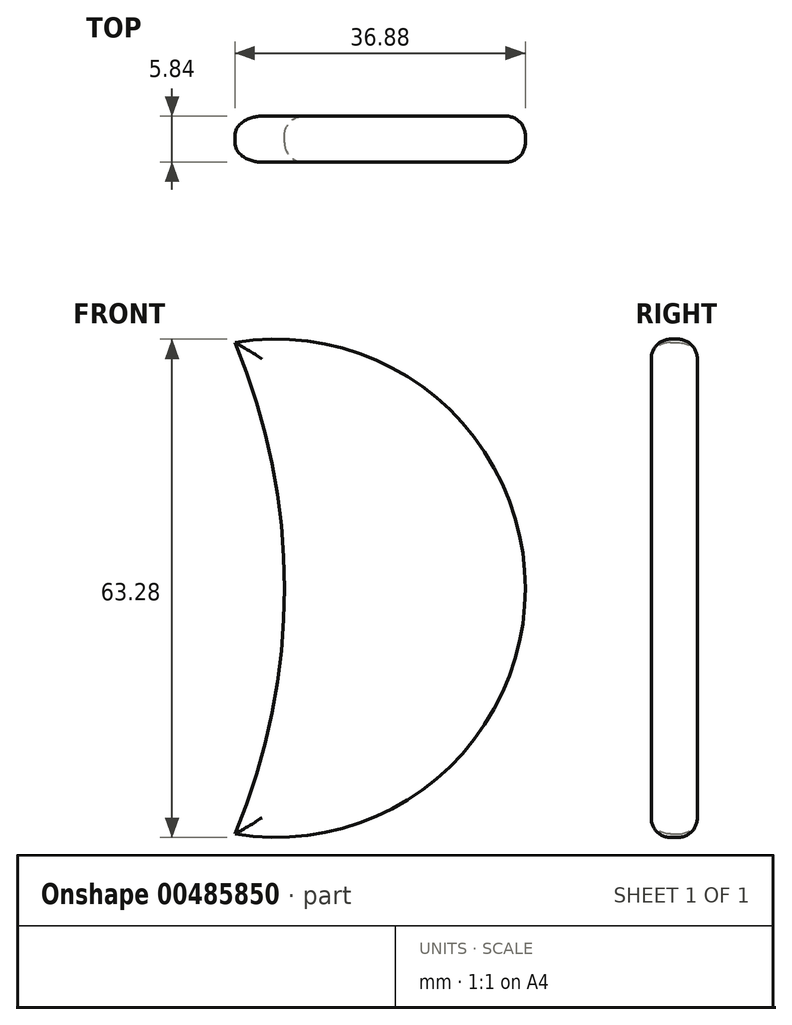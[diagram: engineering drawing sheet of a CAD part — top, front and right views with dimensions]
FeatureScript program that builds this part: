
annotation { "Feature Type Name" : "Feature", "Feature Type Description" : "" }
export const myFeature = defineFeature(function(context is Context, id is Id, definition is map)
    precondition{}
    {
        {
            var Q0;
            Q0=qCreatedBy(makeId("Front.planeOp"),FACE);
            var sketch = newSketch(context, id + "F0", { "sketchPlane" : qUnion([Q0])});
            skArc(sketch, "E0", {"start": v(0, -33.74) * mm, "mid": v(6.29, -2.53) * mm, "end": v(0, 28.68) * mm});
            skArc(sketch, "E1", {"start": v(0, -33.74) * mm, "mid": v(36.88, -2.53) * mm, "end": v(0, 28.68) * mm});
            skSolve(sketch);
        }
        {
            var Q0;
            Q0=makeQuery(id+"F0.imprint","IMPRINT",FACE,{"disambiguationData":[TD([[makeQuery(id+"F0.imprint","IMPRINT",EDGE,{"derivedFrom":sQuery(id+"F0.wireOp",EDGE,"E0")}),-1.0]])]});
            extrude(context, id + "F1", {"entities" : qUnion([Q0]), "depth" : 5.84 * mm});
        }
        {
            var Q0;
            Q0=makeQuery(id+"F1.opExtrude","CAP_EDGE",EDGE,{"disambiguationData":[OSD([sQuery(id+"F0.wireOp",EDGE,"E0")])],"isStart":false});
            var Q1;
            Q1=makeQuery(id+"F1.opExtrude","CAP_EDGE",EDGE,{"disambiguationData":[OSD([sQuery(id+"F0.wireOp",EDGE,"E1")])],"isStart":false});
            var Q2;
            Q2=makeQuery(id+"F1.opExtrude","CAP_EDGE",EDGE,{"disambiguationData":[OSD([sQuery(id+"F0.wireOp",EDGE,"E1")])],"isStart":true});
            var Q3;
            Q3=makeQuery(id+"F1.opExtrude","CAP_EDGE",EDGE,{"disambiguationData":[OSD([sQuery(id+"F0.wireOp",EDGE,"E0")])],"isStart":true});
            fillet(context, id + "F2", {"entities" : qUnion([Q0, Q1, Q2, Q3]), "radius" : 2.45 * mm, "tangentPropagation" : true, "allowEdgeOverflow" : false});
        }
    });
